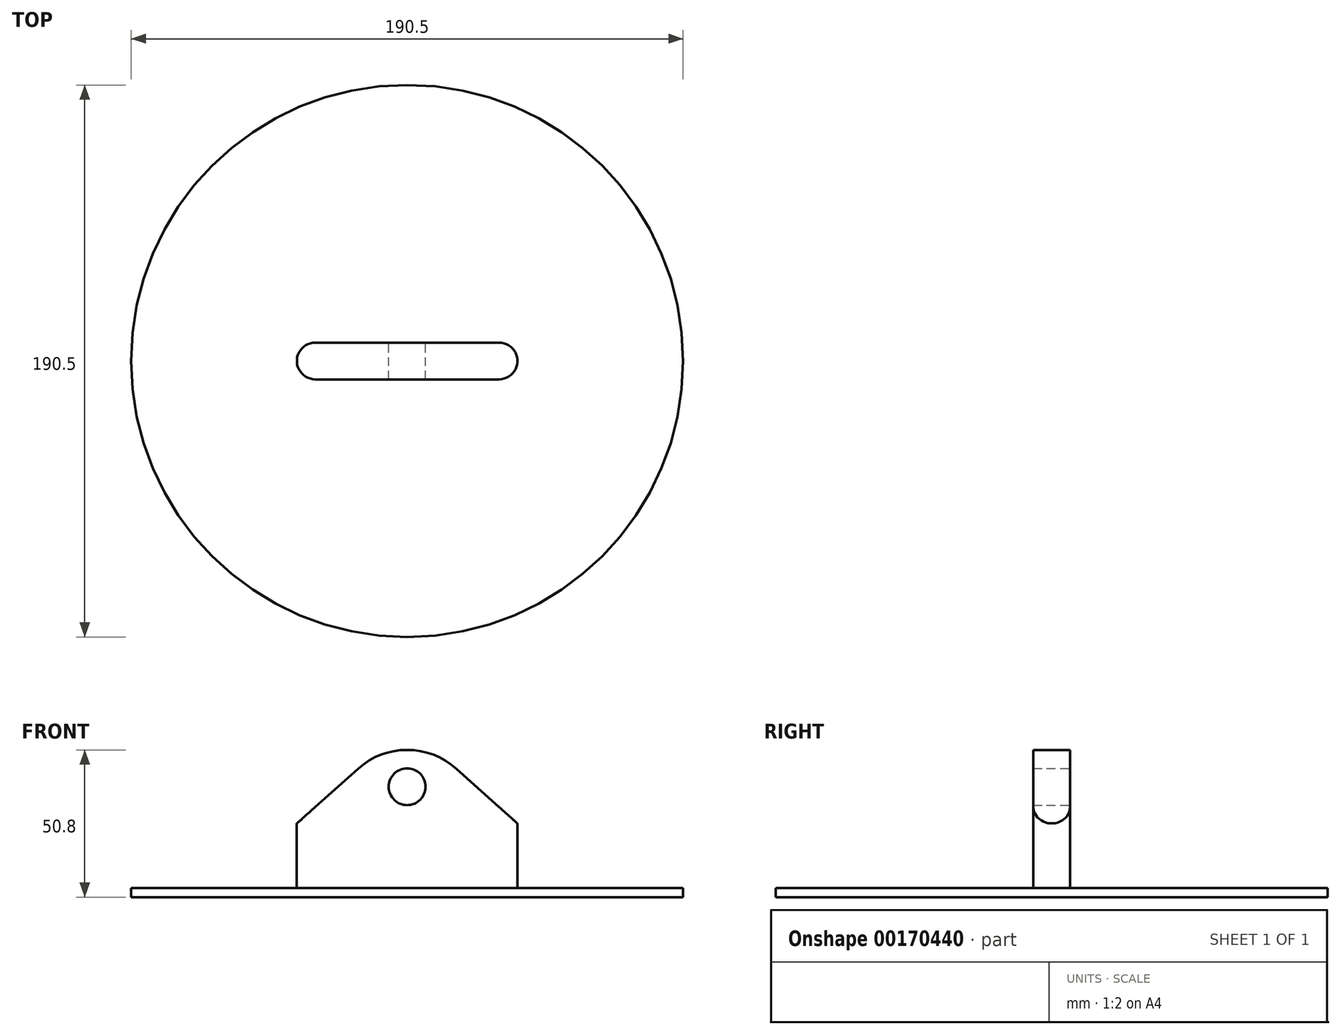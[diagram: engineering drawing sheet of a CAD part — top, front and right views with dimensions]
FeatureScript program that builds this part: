
annotation { "Feature Type Name" : "Feature", "Feature Type Description" : "" }
export const myFeature = defineFeature(function(context is Context, id is Id, definition is map)
    precondition{}
    {
        {
            var Q0;
            Q0=qCreatedBy(makeId("Top.planeOp"),FACE);
            var sketch = newSketch(context, id + "F0", { "sketchPlane" : qUnion([Q0])});
            skCircle(sketch, "E0", {"center": v(0, 0) * mm, "radius": 95.25 * mm});
            skCircle(sketch, "E1", {"center": v(0, 0) * mm, "radius": 98.43 * mm});
            skSolve(sketch);
        }
        {
            var Q0;
            Q0=makeQuery(id+"F0.imprint","IMPRINT",FACE,{"disambiguationData":[TD([[makeQuery(id+"F0.imprint","IMPRINT",EDGE,{"derivedFrom":sQuery(id+"F0.wireOp",EDGE,"E0")}),1.0]])]});
            extrude(context, id + "F1", {"entities" : qUnion([Q0]), "depth" : 3.17 * mm});
        }
        {
            var Q0;
            Q0=qCreatedBy(makeId("Front.planeOp"),FACE);
            var sketch = newSketch(context, id + "F2", { "sketchPlane" : qUnion([Q0])});
            skLineSegment(sketch, "E2.left", {"start": v(38.1, 25.4) * mm, "end": v(38.1, 0) * mm});
            skLineSegment(sketch, "E2.right", {"start": v(-38.1, 25.4) * mm, "end": v(-38.1, 0) * mm});
            skPoint(sketch, "E2.middle", {"position": v(0, 0) * mm});
            skLineSegment(sketch, "E3", {"start": v(-38.1, 0) * mm, "end": v(38.1, 0) * mm});
            skLineSegment(sketch, "E4", {"start": v(-38.1, 25.4) * mm, "end": v(-16.93, 44.33) * mm});
            skLineSegment(sketch, "E5", {"start": v(38.1, 25.4) * mm, "end": v(16.93, 44.33) * mm});
            skArc(sketch, "E6.trimOffspring", {"start": v(16.93, 44.33) * mm, "mid": v(0, 50.8) * mm, "end": v(-16.93, 44.33) * mm});
            skLineSegment(sketch, "E7", {"start": v(0, 0) * mm, "end": v(0, 38.1) * mm});
            skCircle(sketch, "E8", {"center": v(0, 38.1) * mm, "radius": 6.35 * mm});
            skSolve(sketch);
        }
        {
            var Q0;
            {var subQ1=sQuery(id+"F2.wireOp",EDGE,"E2.left");Q0=makeQuery(id+"F2.imprint","IMPRINT",FACE,{"disambiguationData":[TD([[makeQuery(id+"F2.imprint","IMPRINT",EDGE,{"derivedFrom":subQ1}),-1.0]])]});}
            extrude(context, id + "F3", {"entities" : qUnion([Q0]), "operationType" : NewBodyOperationType.ADD, "endBound" : BoundingType.SYMMETRIC, "depth" : 12.7 * mm});
        }
        {
            var Q0;
            Q0=makeQuery(id+"F3.opExtrude","CAP_EDGE",EDGE,{"disambiguationData":[OSD([sQuery(id+"F2.wireOp",EDGE,"E2.right")])],"isStart":false});
            var Q1;
            Q1=makeQuery(id+"F3.opExtrude","CAP_EDGE",EDGE,{"disambiguationData":[OSD([sQuery(id+"F2.wireOp",EDGE,"E2.right")])],"isStart":true});
            var Q2;
            Q2=makeQuery(id+"F3.opExtrude","CAP_EDGE",EDGE,{"disambiguationData":[OSD([sQuery(id+"F2.wireOp",EDGE,"E2.left")])],"isStart":false});
            var Q3;
            Q3=makeQuery(id+"F3.opExtrude","CAP_EDGE",EDGE,{"disambiguationData":[OSD([sQuery(id+"F2.wireOp",EDGE,"E2.left")])],"isStart":true});
            fillet(context, id + "F4", {"entities" : qUnion([Q0, Q1, Q2, Q3]), "radius" : 6.35 * mm, "tangentPropagation" : true, "allowEdgeOverflow" : false});
        }
    });
